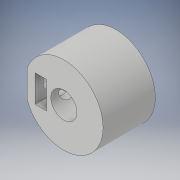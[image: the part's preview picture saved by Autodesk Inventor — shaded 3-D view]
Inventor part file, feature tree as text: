
AUTODESK INVENTOR PART (.ipt)
format: ipt  version: 2019 (Build 230136000, 136)  size: 135,168 bytes
history: native  units: mm
features: extrude x4, sketch x4, plane x1
ambient origin geometry x8: Origin, YZ Plane, XZ Plane, XY Plane, X Axis, Y Axis, Z Axis, Center Point
bodies: Solid1 (feature_tree)
feature tree (9):
  extrude  "Extrusion1"  Depth=5.0mm
  plane  "Work Plane1"
  extrude  "Extrusion2"  Depth=10.0mm
  extrude  "Extrusion3"  Depth=2.2mm
  extrude  "Extrusion4"  Depth=10.0mm TaperAngle=0.0deg
  sketch  "Sketch1"  dims[d0=15.0mm d1=5.0mm]
  sketch  "Sketch2"  dims[d2=10.0mm d3=0.0mm d4=5.0mm]
  sketch  "Sketch4"  dims[d5=5.5mm d6=2.2mm]
  sketch  "Sketch5"  dims[d7=5.2mm d8=5.0mm d9=0.0mm d12=3.0mm d13=7.0mm d14=8.0mm d15=0.0mm d16=6.0mm d17=10.0mm d18=0.5mm d19=8.0mm d20=0.0mm]
